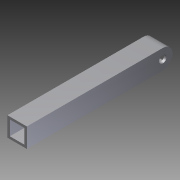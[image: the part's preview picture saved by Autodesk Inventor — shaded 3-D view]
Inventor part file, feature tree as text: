
AUTODESK INVENTOR PART (.ipt)
format: ipt  version: 2012 (Build 160160000, 160)  size: 96,768 bytes
history: native  units: in
note: dims shown in document units (in); Inventor stores cm internally (conversion verified against a paired STEP export)
features: extrude x2, sketch x2
ambient origin geometry x8: Origin, YZ Plane, XZ Plane, XY Plane, X Axis, Y Axis, Z Axis, Center Point
bodies: Solid1 (feature_tree)
feature tree (4):
  extrude  "Extrusion1"  Depth=1.0in
  extrude  "Extrusion2"  Depth=0.125in
  sketch  "Sketch1"  dims[d0=1.0in d1=1.0in]
  sketch  "Sketch2"  dims[d2=0.125in d3=0.125in d4=0.125in d5=0.125in d6=7.5in d7=0.0in d8=0.375in d9=0.5in d10=0.5in d11=1.0in d12=0.0in]
